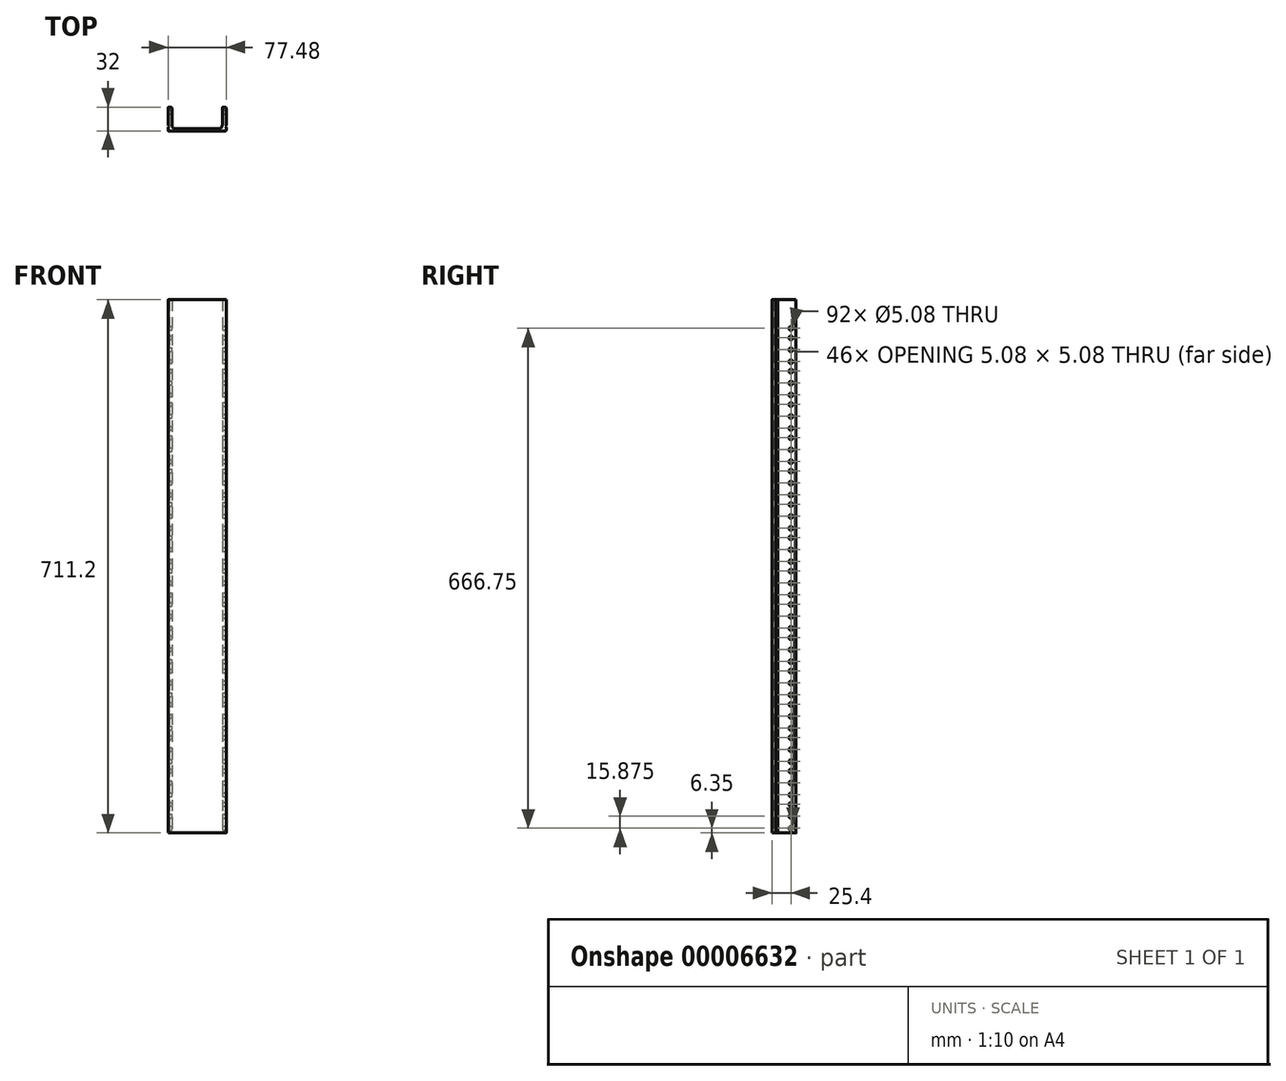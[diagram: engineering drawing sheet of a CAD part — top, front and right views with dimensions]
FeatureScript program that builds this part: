
annotation { "Feature Type Name" : "Feature", "Feature Type Description" : "" }
export const myFeature = defineFeature(function(context is Context, id is Id, definition is map)
    precondition{}
    {
        {
            var Q0;
            Q0=qCreatedBy(makeId("Top.planeOp"),FACE);
            var sketch = newSketch(context, id + "F0", { "sketchPlane" : qUnion([Q0])});
            skLineSegment(sketch, "E0", {"start": v(-37.46, 0) * mm, "end": v(37.46, 0) * mm});
            skLineSegment(sketch, "E1", {"start": v(-43.23, 6.35) * mm, "end": v(40.73, 6.35) * mm, "construction": true});
            skLineSegment(sketch, "E2", {"start": v(-38.73, 1.27) * mm, "end": v(-38.73, 5.08) * mm});
            skLineSegment(sketch, "E3", {"start": v(-37.47, 32) * mm, "end": v(-34.92, 32) * mm});
            skLineSegment(sketch, "E4", {"start": v(-33.65, 30.73) * mm, "end": v(-33.65, 8) * mm});
            skLineSegment(sketch, "E5", {"start": v(-28.57, 2.92) * mm, "end": v(28.57, 2.92) * mm});
            skLineSegment(sketch, "E6", {"start": v(33.65, 8) * mm, "end": v(33.65, 30.73) * mm});
            skLineSegment(sketch, "E7", {"start": v(34.92, 32) * mm, "end": v(37.46, 32) * mm});
            skLineSegment(sketch, "E8", {"start": v(38.73, 30.73) * mm, "end": v(38.73, 7.62) * mm});
            skPoint(sketch, "E9.visualSharp", {"position": v(-33.65, 2.92) * mm});
            skArc(sketch, "E9.filletArc", {"start": v(-33.65, 8) * mm, "mid": v(-32.17, 4.4) * mm, "end": v(-28.57, 2.92) * mm});
            skPoint(sketch, "E10.visualSharp", {"position": v(33.65, 2.92) * mm});
            skArc(sketch, "E10.filletArc", {"start": v(28.57, 2.92) * mm, "mid": v(32.17, 4.4) * mm, "end": v(33.65, 8) * mm});
            skPoint(sketch, "E11.visualSharp", {"position": v(-38.73, 0) * mm});
            skArc(sketch, "E11.filletArc", {"start": v(-38.73, 1.27) * mm, "mid": v(-38.36, 0.37) * mm, "end": v(-37.46, 0) * mm});
            skPoint(sketch, "E12.visualSharp", {"position": v(38.73, 0) * mm});
            skArc(sketch, "E12.filletArc", {"start": v(37.46, 0) * mm, "mid": v(38.36, 0.37) * mm, "end": v(38.73, 1.27) * mm});
            skPoint(sketch, "E13.visualSharp", {"position": v(38.73, 32) * mm});
            skArc(sketch, "E13.filletArc", {"start": v(38.73, 30.73) * mm, "mid": v(38.36, 31.63) * mm, "end": v(37.46, 32) * mm});
            skPoint(sketch, "E14.visualSharp", {"position": v(33.65, 32) * mm});
            skArc(sketch, "E14.filletArc", {"start": v(34.92, 32) * mm, "mid": v(34.03, 31.63) * mm, "end": v(33.65, 30.73) * mm});
            skPoint(sketch, "E15.visualSharp", {"position": v(-38.73, 32) * mm});
            skArc(sketch, "E15.filletArc", {"start": v(-37.47, 32) * mm, "mid": v(-38.36, 31.63) * mm, "end": v(-38.73, 30.73) * mm});
            skPoint(sketch, "E16.visualSharp", {"position": v(-33.65, 32) * mm});
            skArc(sketch, "E16.filletArc", {"start": v(-33.65, 30.73) * mm, "mid": v(-34.03, 31.63) * mm, "end": v(-34.92, 32) * mm});
            skLineSegment(sketch, "E17", {"start": v(-38.74, 7.62) * mm, "end": v(-37.46, 6.35) * mm});
            skLineSegment(sketch, "E18", {"start": v(-37.46, 6.35) * mm, "end": v(-38.73, 5.08) * mm});
            skLineSegment(sketch, "E19.trimOffspring", {"start": v(-38.73, 7.62) * mm, "end": v(-38.73, 30.73) * mm});
            skLineSegment(sketch, "E20.0.MirrorCS", {"start": v(38.74, 7.62) * mm, "end": v(37.46, 6.35) * mm});
            skLineSegment(sketch, "E21.0.MirrorCS", {"start": v(37.46, 6.35) * mm, "end": v(38.73, 5.08) * mm});
            skLineSegment(sketch, "E22.trimOffspring", {"start": v(38.73, 5.08) * mm, "end": v(38.73, 1.27) * mm});
            skSolve(sketch);
        }
        {
            var Q0;
            Q0=makeQuery(id+"F0.imprint","IMPRINT",FACE,{"disambiguationData":[TD([[makeQuery(id+"F0.imprint","IMPRINT",EDGE,{"derivedFrom":sQuery(id+"F0.wireOp",EDGE,"E0")}),1.0]])]});
            extrude(context, id + "F1", {"entities" : qUnion([Q0]), "depth" : 711.2 * mm});
        }
        {
            var Q0;
            Q0=makeQuery(id+"F1.opExtrude","SWEPT_FACE",FACE,{"disambiguationData":[OSD([sQuery(id+"F0.wireOp",EDGE,"E8")])]});
            var sketch = newSketch(context, id + "F2", { "sketchPlane" : qUnion([Q0])});
            skLineSegment(sketch, "E23", {"start": v(25.4, -14.2) * mm, "end": v(25.4, 90.4) * mm, "construction": true});
            skCircle(sketch, "E24", {"center": v(25.4, 6.35) * mm, "radius": 2.54 * mm});
            skCircle(sketch, "E25", {"center": v(25.4, 22.23) * mm, "radius": 2.54 * mm});
            skCircle(sketch, "E26", {"center": v(25.4, 38.1) * mm, "radius": 2.54 * mm});
            skCircle(sketch, "E27", {"center": v(25.4, 50.8) * mm, "radius": 2.54 * mm});
            skCircle(sketch, "E28.0.1.0", {"center": v(25.4, 66.68) * mm, "radius": 2.54 * mm});
            skCircle(sketch, "E28.0.1.1", {"center": v(25.4, 82.55) * mm, "radius": 2.54 * mm});
            skCircle(sketch, "E28.0.1.2", {"center": v(25.4, 95.25) * mm, "radius": 2.54 * mm});
            skCircle(sketch, "E28.0.2.0", {"center": v(25.4, 111.13) * mm, "radius": 2.54 * mm});
            skCircle(sketch, "E28.0.2.1", {"center": v(25.4, 127) * mm, "radius": 2.54 * mm});
            skCircle(sketch, "E28.0.2.2", {"center": v(25.4, 139.7) * mm, "radius": 2.54 * mm});
            skCircle(sketch, "E28.0.3.0", {"center": v(25.4, 155.58) * mm, "radius": 2.54 * mm});
            skCircle(sketch, "E28.0.3.1", {"center": v(25.4, 171.45) * mm, "radius": 2.54 * mm});
            skCircle(sketch, "E28.0.3.2", {"center": v(25.4, 184.15) * mm, "radius": 2.54 * mm});
            skCircle(sketch, "E28.0.4.0", {"center": v(25.4, 200.03) * mm, "radius": 2.54 * mm});
            skCircle(sketch, "E28.0.4.1", {"center": v(25.4, 215.9) * mm, "radius": 2.54 * mm});
            skCircle(sketch, "E28.0.4.2", {"center": v(25.4, 228.6) * mm, "radius": 2.54 * mm});
            skCircle(sketch, "E28.0.5.0", {"center": v(25.4, 244.48) * mm, "radius": 2.54 * mm});
            skCircle(sketch, "E28.0.5.1", {"center": v(25.4, 260.35) * mm, "radius": 2.54 * mm});
            skCircle(sketch, "E28.0.5.2", {"center": v(25.4, 273.05) * mm, "radius": 2.54 * mm});
            skCircle(sketch, "E28.0.6.0", {"center": v(25.4, 288.93) * mm, "radius": 2.54 * mm});
            skCircle(sketch, "E28.0.6.1", {"center": v(25.4, 304.8) * mm, "radius": 2.54 * mm});
            skCircle(sketch, "E28.0.6.2", {"center": v(25.4, 317.5) * mm, "radius": 2.54 * mm});
            skCircle(sketch, "E28.0.7.0", {"center": v(25.4, 333.38) * mm, "radius": 2.54 * mm});
            skCircle(sketch, "E28.0.7.1", {"center": v(25.4, 349.25) * mm, "radius": 2.54 * mm});
            skCircle(sketch, "E28.0.7.2", {"center": v(25.4, 361.95) * mm, "radius": 2.54 * mm});
            skCircle(sketch, "E28.0.8.0", {"center": v(25.4, 377.83) * mm, "radius": 2.54 * mm});
            skCircle(sketch, "E28.0.8.1", {"center": v(25.4, 393.7) * mm, "radius": 2.54 * mm});
            skCircle(sketch, "E28.0.8.2", {"center": v(25.4, 406.4) * mm, "radius": 2.54 * mm});
            skCircle(sketch, "E28.0.9.0", {"center": v(25.4, 422.28) * mm, "radius": 2.54 * mm});
            skCircle(sketch, "E28.0.9.1", {"center": v(25.4, 438.15) * mm, "radius": 2.54 * mm});
            skCircle(sketch, "E28.0.9.2", {"center": v(25.4, 450.85) * mm, "radius": 2.54 * mm});
            skCircle(sketch, "E28.0.10.0", {"center": v(25.4, 466.73) * mm, "radius": 2.54 * mm});
            skCircle(sketch, "E28.0.10.1", {"center": v(25.4, 482.6) * mm, "radius": 2.54 * mm});
            skCircle(sketch, "E28.0.10.2", {"center": v(25.4, 495.3) * mm, "radius": 2.54 * mm});
            skCircle(sketch, "E28.0.11.0", {"center": v(25.4, 511.18) * mm, "radius": 2.54 * mm});
            skCircle(sketch, "E28.0.11.1", {"center": v(25.4, 527.05) * mm, "radius": 2.54 * mm});
            skCircle(sketch, "E28.0.11.2", {"center": v(25.4, 539.75) * mm, "radius": 2.54 * mm});
            skCircle(sketch, "E28.0.12.0", {"center": v(25.4, 555.63) * mm, "radius": 2.54 * mm});
            skCircle(sketch, "E28.0.12.1", {"center": v(25.4, 571.5) * mm, "radius": 2.54 * mm});
            skCircle(sketch, "E28.0.12.2", {"center": v(25.4, 584.2) * mm, "radius": 2.54 * mm});
            skCircle(sketch, "E28.0.13.0", {"center": v(25.4, 600.08) * mm, "radius": 2.54 * mm});
            skCircle(sketch, "E28.0.13.1", {"center": v(25.4, 615.95) * mm, "radius": 2.54 * mm});
            skCircle(sketch, "E28.0.13.2", {"center": v(25.4, 628.65) * mm, "radius": 2.54 * mm});
            skCircle(sketch, "E28.0.14.0", {"center": v(25.4, 644.53) * mm, "radius": 2.54 * mm});
            skCircle(sketch, "E28.0.14.1", {"center": v(25.4, 660.4) * mm, "radius": 2.54 * mm});
            skCircle(sketch, "E28.0.14.2", {"center": v(25.4, 673.1) * mm, "radius": 2.54 * mm});
            skLineSegment(sketch, "E28.direction1", {"start": v(25.4, 22.23) * mm, "end": v(41.27, 22.23) * mm, "construction": true});
            skLineSegment(sketch, "E28.direction2", {"start": v(25.4, 22.23) * mm, "end": v(25.4, 66.68) * mm, "construction": true});
            skSolve(sketch);
        }
        {
            var Q0;
            Q0 = qSketchRegion(id + "F2", true);
            extrude(context, id + "F3", {"entities" : qUnion([Q0]), "operationType" : NewBodyOperationType.REMOVE, "oppositeDirection" : true, "depth" : 78.74 * mm});
        }
    });
